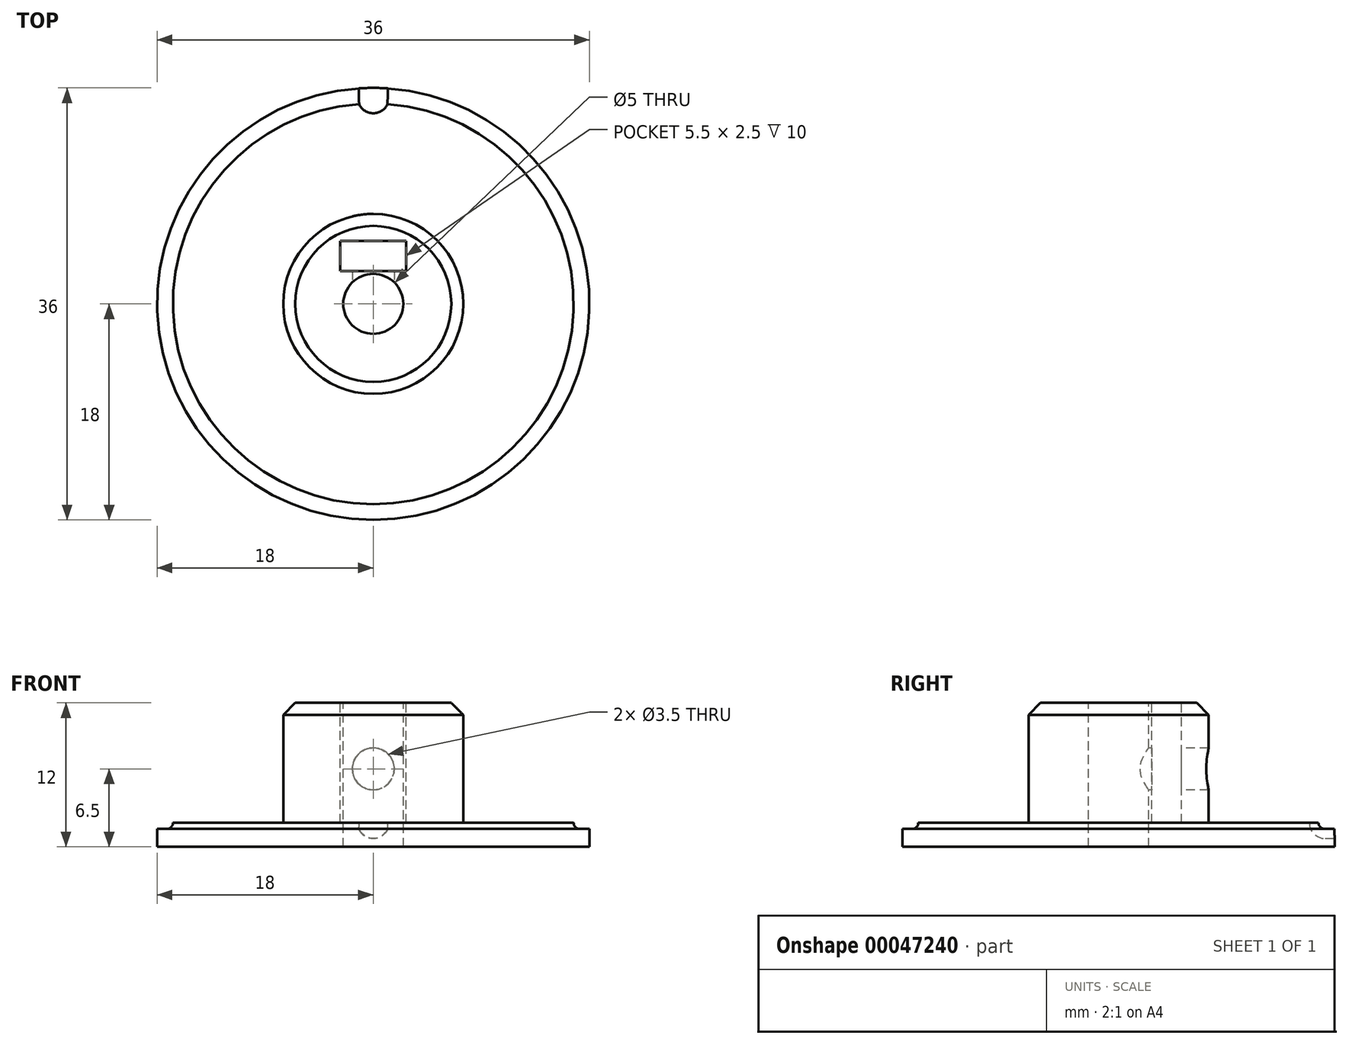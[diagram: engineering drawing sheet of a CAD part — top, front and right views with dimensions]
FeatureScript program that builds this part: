
annotation { "Feature Type Name" : "Feature", "Feature Type Description" : "" }
export const myFeature = defineFeature(function(context is Context, id is Id, definition is map)
    precondition{}
    {
        {
            var Q0;
            Q0=qCreatedBy(makeId("Top.planeOp"),FACE);
            var sketch = newSketch(context, id + "F0", { "sketchPlane" : qUnion([Q0])});
            skCircle(sketch, "E0", {"center": v(0, 0) * mm, "radius": 17.19 * mm});
            skLineSegment(sketch, "E1", {"start": v(0, 0) * mm, "end": v(0, 17.19) * mm});
            skCircle(sketch, "E2", {"center": v(0, 17.19) * mm, "radius": 1.3 * mm});
            skCircle(sketch, "E3", {"center": v(0, 0) * mm, "radius": 18 * mm});
            skSolve(sketch);
        }
        {
            var Q0;
            Q0=qCreatedBy(makeId("Top.planeOp"),FACE);
            var sketch = newSketch(context, id + "F1", { "sketchPlane" : qUnion([Q0])});
            skSolve(sketch);
        }
        {
            var Q0;
            Q0 = qSketchRegion(id + "F1", true);
            var Q1;
            {var subQ0=sQuery(id+"F0.wireOp",EDGE,"E2");var subQ1=sQuery(id+"F0.wireOp",EDGE,"E0");var subQ2=makeQuery(id+"F0.imprint","INTERSECT",VERTEX,{"disambiguationData":[OD(0.0)],"derivedFrom":[subQ1,subQ0]});Q1=makeQuery(id+"F0.imprint","IMPRINT",FACE,{"disambiguationData":[TD([[makeQuery(id+"F0.imprint","IMPRINT",EDGE,{"disambiguationData":[TD([[subQ2,1.0]])],"derivedFrom":subQ1}),1.0]])]});}
            var Q2;
            {var subQ0=sQuery(id+"F0.wireOp",EDGE,"E1");var subQ1=sQuery(id+"F0.wireOp",EDGE,"E0");var subQ2=makeQuery(id+"F0.imprint","INTERSECT",VERTEX,{"derivedFrom":[subQ1,subQ0]});Q2=makeQuery(id+"F0.imprint","IMPRINT",FACE,{"disambiguationData":[TD([[makeQuery(id+"F0.imprint","IMPRINT",EDGE,{"disambiguationData":[TD([[subQ2,-1.0]])],"derivedFrom":subQ1}),1.0]])]});}
            var Q3;
            {var subQ0=sQuery(id+"F0.wireOp",EDGE,"E1");var subQ1=sQuery(id+"F0.wireOp",EDGE,"E0");var subQ2=makeQuery(id+"F0.imprint","INTERSECT",VERTEX,{"derivedFrom":[subQ1,subQ0]});Q3=makeQuery(id+"F0.imprint","IMPRINT",FACE,{"disambiguationData":[TD([[makeQuery(id+"F0.imprint","IMPRINT",EDGE,{"disambiguationData":[TD([[subQ2,1.0]])],"derivedFrom":subQ1}),1.0]])]});}
            var Q4;
            {var subQ0=sQuery(id+"F0.wireOp",EDGE,"E2");var subQ1=sQuery(id+"F0.wireOp",EDGE,"E0");var subQ2=makeQuery(id+"F0.imprint","INTERSECT",VERTEX,{"disambiguationData":[OD(0.0)],"derivedFrom":[subQ1,subQ0]});Q4=makeQuery(id+"F0.imprint","IMPRINT",FACE,{"disambiguationData":[TD([[makeQuery(id+"F0.imprint","IMPRINT",EDGE,{"disambiguationData":[TD([[subQ2,1.0]])],"derivedFrom":subQ1}),-1.0]])]});}
            var Q5;
            {var subQ3=sQuery(id+"F0.wireOp",EDGE,"E0");var subQ5=makeQuery(id+"F0.imprint","INTERSECT",VERTEX,{"derivedFrom":[subQ3,sQuery(id+"F0.wireOp",EDGE,"E1")]});Q5=makeQuery(id+"F0.imprint","IMPRINT",FACE,{"disambiguationData":[TD([[makeQuery(id+"F0.imprint","IMPRINT",EDGE,{"disambiguationData":[TD([[subQ5,1.0]])],"derivedFrom":subQ3}),-1.0]])]});}
            extrude(context, id + "F2", {"entities" : qUnion([Q0, Q1, Q2, Q3, Q4, Q5]), "depth" : 4 * mm});
        }
        {
            var Q0;
            Q0=qCreatedBy(makeId("Top.planeOp"),FACE);
            var Q1;
            Q1=makeQuery(id+"F2.opExtrude","CAP_FACE",FACE,{"disambiguationData":[OSD([sQuery(id+"F0.wireOp",EDGE,"E3")])],"isStart":false});
            cPlane(context, id + "F3", {"entities" : qUnion([Q0, Q1]), "cplaneType" : CPlaneType.MID_PLANE, "offset" : 25 * mm, "width" : 150 * mm, "height" : 150 * mm});
        }
        {
            var Q0;
            Q0=qCreatedBy(id+"F3.planeOp",FACE);
            var sketch = newSketch(context, id + "F4", { "sketchPlane" : qUnion([Q0])});
            skArc(sketch, "E4.0", {"start": v(0, 15.89) * mm, "mid": v(1.3, 17.19) * mm, "end": v(0, 18.49) * mm});
            skLineSegment(sketch, "E5", {"start": v(0, 15.89) * mm, "end": v(0, 18.49) * mm});
            skLineSegment(sketch, "E6", {"start": v(0, 17.19) * mm, "end": v(1.3, 17.19) * mm});
            skLineSegment(sketch, "E7", {"start": v(1.3, 17.19) * mm, "end": v(1.3, 18.49) * mm});
            skLineSegment(sketch, "E8", {"start": v(1.3, 18.49) * mm, "end": v(0, 18.49) * mm});
            skSolve(sketch);
        }
        {
            var Q0;
            Q0=makeQuery(id+"F4.imprint","IMPRINT",FACE,{"disambiguationData":[TD([[makeQuery(id+"F4.imprint","IMPRINT",EDGE,{"derivedFrom":sQuery(id+"F4.wireOp",EDGE,"E4.0")}),1.0]])]});
            var Q1;
            {var subQ2=sQuery(id+"F4.wireOp",EDGE,"E7");Q1=makeQuery(id+"F4.imprint","IMPRINT",FACE,{"disambiguationData":[TD([[makeQuery(id+"F4.imprint","IMPRINT",EDGE,{"derivedFrom":subQ2}),1.0]])]});}
            var Q2;
            Q2=sQuery(id+"F4.wireOp",EDGE,"E5");
            revolve(context, id + "F5", {"operationType" : NewBodyOperationType.REMOVE, "entities" : qUnion([Q0, Q1]), "axis" : qUnion([Q2]), "revolveType" : RevolveType.FULL, "oppositeDirection" : true});
        }
        {
            var Q0;
            Q0=qCreatedBy(makeId("Front.planeOp"),FACE);
            var sketch = newSketch(context, id + "F6", { "sketchPlane" : qUnion([Q0])});
            skLineSegment(sketch, "E9.0", {"start": v(-17.19, 4) * mm, "end": v(17.19, 4) * mm, "construction": true});
            skLineSegment(sketch, "E9.1", {"start": v(-17.19, 0) * mm, "end": v(17.19, 0) * mm, "construction": true});
            skLineSegment(sketch, "E10", {"start": v(0, 0) * mm, "end": v(0, 4) * mm, "construction": true});
            skLineSegment(sketch, "E11", {"start": v(0, 2) * mm, "end": v(17.19, 2) * mm, "construction": true});
            skArc(sketch, "E12", {"start": v(17.19, 2.5) * mm, "mid": v(16.69, 2) * mm, "end": v(17.19, 1.5) * mm});
            skLineSegment(sketch, "E13", {"start": v(16.69, 2) * mm, "end": v(16.56, 2) * mm, "construction": true});
            skLineSegment(sketch, "E14", {"start": v(17.19, 2.5) * mm, "end": v(18.21, 2.5) * mm});
            skLineSegment(sketch, "E15", {"start": v(18.21, 2.5) * mm, "end": v(18.21, 1.5) * mm});
            skLineSegment(sketch, "E16", {"start": v(17.19, 1.5) * mm, "end": v(18.21, 1.5) * mm});
            skSolve(sketch);
        }
        {
            var Q0;
            {var subQ1=sQuery(id+"F6.wireOp",EDGE,"E12");var subQ6=sQuery(id+"F6.wireOp",EDGE,"Q5owe86Z-UdA3-Mzv4-9Ln9-rBpZI1dkmUp1");var subQ8=makeQuery(id+"F6.imprint","INTERSECT",VERTEX,{"disambiguationData":[OD(0.0)],"derivedFrom":[subQ1,subQ6]});Q0=makeQuery(id+"F6.imprint","IMPRINT",FACE,{"disambiguationData":[TD([[makeQuery(id+"F6.imprint","IMPRINT",EDGE,{"disambiguationData":[TD([[subQ8,1.0]])],"derivedFrom":subQ1}),1.0]])]});}
            var Q1;
            {var subQ0=sQuery(id+"F6.wireOp",EDGE,"Q5owe86Z-UdA3-Mzv4-9Ln9-rBpZI1dkmUp1");var subQ1=sQuery(id+"F6.wireOp",EDGE,"E12");var subQ2=makeQuery(id+"F6.imprint","INTERSECT",VERTEX,{"disambiguationData":[OD(0.0)],"derivedFrom":[subQ1,subQ0]});Q1=makeQuery(id+"F6.imprint","IMPRINT",FACE,{"disambiguationData":[TD([[makeQuery(id+"F6.imprint","IMPRINT",EDGE,{"disambiguationData":[TD([[subQ2,1.0]])],"derivedFrom":subQ1}),-1.0]])]});}
            var Q2;
            {var subQ0=sQuery(id+"F6.wireOp",EDGE,"TDUslP9x-rfeX-e3iP-snPt-IsEtmXCtfriO");var subQ1=sQuery(id+"F6.wireOp",EDGE,"E12");var subQ2=makeQuery(id+"F6.imprint","INTERSECT",VERTEX,{"disambiguationData":[OD(1.0)],"derivedFrom":[subQ1,subQ0]});Q2=makeQuery(id+"F6.imprint","IMPRINT",FACE,{"disambiguationData":[TD([[makeQuery(id+"F6.imprint","IMPRINT",EDGE,{"disambiguationData":[TD([[subQ2,-1.0]])],"derivedFrom":subQ1}),-1.0]])]});}
            var Q3;
            Q3=sQuery(id+"F0.wireOp",EDGE,"E0");
            revolve(context, id + "F7", {"operationType" : NewBodyOperationType.REMOVE, "entities" : qUnion([Q0, Q1, Q2]), "axis" : qUnion([Q3]), "revolveType" : RevolveType.FULL, "oppositeDirection" : true});
        }
        {
            var Q0;
            Q0=makeQuery(id+"F2.opExtrude","CAP_FACE",FACE,{"disambiguationData":[OSD([sQuery(id+"F0.wireOp",EDGE,"E3")])],"isStart":false});
            var sketch = newSketch(context, id + "F8", { "sketchPlane" : qUnion([Q0])});
            skCircle(sketch, "E17", {"center": v(0, 0) * mm, "radius": 2.5 * mm});
            skSolve(sketch);
        }
        {
            var Q0;
            Q0 = qSketchRegion(id + "F8", true);
            extrude(context, id + "F9", {"entities" : qUnion([Q0]), "operationType" : NewBodyOperationType.REMOVE, "oppositeDirection" : true, "depth" : 25 * mm});
        }
        {
            var Q0;
            Q0=makeQuery(id+"F2.opExtrude","CAP_FACE",FACE,{"disambiguationData":[OSD([sQuery(id+"F0.wireOp",EDGE,"E3")])],"isStart":false});
            var sketch = newSketch(context, id + "F10", { "sketchPlane" : qUnion([Q0])});
            skCircle(sketch, "E18", {"center": v(0, 0) * mm, "radius": 56.26 * mm});
            skSolve(sketch);
        }
        {
            var Q0;
            Q0 = qSketchRegion(id + "F10", true);
            extrude(context, id + "F11", {"entities" : qUnion([Q0]), "operationType" : NewBodyOperationType.REMOVE, "oppositeDirection" : true, "depth" : 2 * mm});
        }
        {
            var Q0;
            Q0=makeQuery(id+"F11.boolean.opBoolean","COPY",FACE,{"derivedFrom":makeQuery(id+"F11.opExtrude","CAP_FACE",FACE,{"disambiguationData":[OSD([sQuery(id+"F10.wireOp",EDGE,"E18")])],"isStart":false})});
            var sketch = newSketch(context, id + "F12", { "sketchPlane" : qUnion([Q0])});
            skCircle(sketch, "E19", {"center": v(0, 0) * mm, "radius": 7.5 * mm});
            skSolve(sketch);
        }
        {
            var Q0;
            Q0=makeQuery(id+"F12.imprint","IMPRINT",FACE,{"disambiguationData":[TD([[makeQuery(id+"F12.imprint","IMPRINT",EDGE,{"derivedFrom":sQuery(id+"F12.wireOp",EDGE,"E19")}),1.0]])]});
            extrude(context, id + "F13", {"entities" : qUnion([Q0]), "operationType" : NewBodyOperationType.ADD, "depth" : 10 * mm});
        }
        {
            var Q0;
            Q0=makeQuery(id+"F13.opExtrude","CAP_EDGE",EDGE,{"disambiguationData":[OSD([sQuery(id+"F12.wireOp",EDGE,"E19")])],"isStart":false});
            chamfer(context, id + "F14", {"entities" : qUnion([Q0]), "width" : 1 * mm, "tangentPropagation" : true});
        }
        {
            var Q0;
            Q0=qCreatedBy(makeId("Front.planeOp"),FACE);
            var sketch = newSketch(context, id + "F15", { "sketchPlane" : qUnion([Q0])});
            skLineSegment(sketch, "E20", {"start": v(0, 0) * mm, "end": v(0, 2) * mm, "construction": true});
            skLineSegment(sketch, "E21.0", {"start": v(7.5, 11) * mm, "end": v(-7.5, 11) * mm, "construction": true});
            skLineSegment(sketch, "E22", {"start": v(0, 2) * mm, "end": v(0, 11) * mm, "construction": true});
            skCircle(sketch, "E23", {"center": v(0, 6.5) * mm, "radius": 1.75 * mm});
            skSolve(sketch);
        }
        {
            var Q0;
            Q0 = qSketchRegion(id + "F15", true);
            extrude(context, id + "F16", {"entities" : qUnion([Q0]), "operationType" : NewBodyOperationType.REMOVE, "oppositeDirection" : true, "depth" : 25 * mm});
        }
        {
            var Q0;
            Q0=makeQuery(id+"F13.opExtrude","CAP_FACE",FACE,{"disambiguationData":[OSD([sQuery(id+"F8.wireOp",EDGE,"E17"),sQuery(id+"F10.wireOp",EDGE,"E18"),sQuery(id+"F12.wireOp",EDGE,"E19")])],"isStart":false});
            var sketch = newSketch(context, id + "F17", { "sketchPlane" : qUnion([Q0])});
            skCircle(sketch, "E24.0", {"center": v(0, 0) * mm, "radius": 7.5 * mm, "construction": true});
            skCircle(sketch, "E24.1", {"center": v(0, 0) * mm, "radius": 2.5 * mm, "construction": true});
            skLineSegment(sketch, "E25", {"start": v(0, 0) * mm, "end": v(2.75, 0) * mm, "construction": true});
            skLineSegment(sketch, "E26", {"start": v(2.75, 2.75) * mm, "end": v(2.75, 5.25) * mm});
            skLineSegment(sketch, "E27", {"start": v(0, 0) * mm, "end": v(-2.75, 0) * mm, "construction": true});
            skLineSegment(sketch, "E28", {"start": v(-2.75, 2.75) * mm, "end": v(-2.75, 5.25) * mm});
            skLineSegment(sketch, "E29", {"start": v(0, 4) * mm, "end": v(0, 2.75) * mm, "construction": true});
            skLineSegment(sketch, "E30", {"start": v(0, 2.75) * mm, "end": v(2.75, 2.75) * mm});
            skLineSegment(sketch, "E31", {"start": v(0, 2.75) * mm, "end": v(-2.75, 2.75) * mm});
            skLineSegment(sketch, "E32", {"start": v(0, 4) * mm, "end": v(0, 5.25) * mm, "construction": true});
            skLineSegment(sketch, "E33", {"start": v(0, 5.25) * mm, "end": v(2.75, 5.25) * mm});
            skLineSegment(sketch, "E34", {"start": v(0, 5.25) * mm, "end": v(-2.75, 5.25) * mm});
            skLineSegment(sketch, "E35", {"start": v(0, 0) * mm, "end": v(0, 4) * mm, "construction": true});
            skSolve(sketch);
        }
        {
            var Q0;
            Q0 = qSketchRegion(id + "F17", true);
            extrude(context, id + "F18", {"entities" : qUnion([Q0]), "operationType" : NewBodyOperationType.REMOVE, "oppositeDirection" : true, "depth" : 10 * mm});
        }
    });
